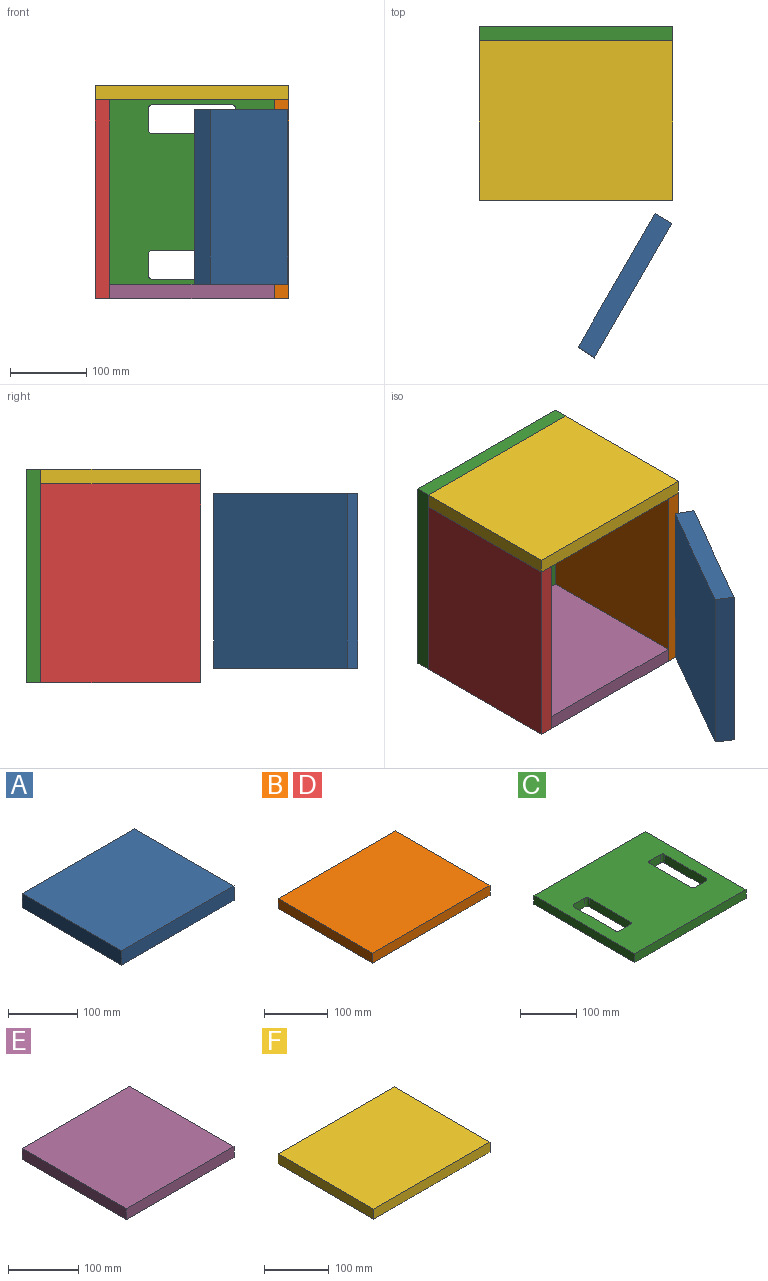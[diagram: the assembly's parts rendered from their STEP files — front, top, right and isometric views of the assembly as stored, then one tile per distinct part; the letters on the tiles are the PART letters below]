
ASSEMBLY  parts=6 mates=5
PART A: 6 faces, bbox 228.6x203.2x25.4 mm
  f0: plane 203.2x25.4mm, normal (-1,0,0), area 5143.3mm2, adj f1,f2,f4,f5
  f1: plane 228.6x201.78mm, normal (0,0,1), area 46127.9mm2, adj f0,f2,f3,f5
  f2: plane 228.6x25.4mm, normal (0,-1,0), area 5806.4mm2, adj f0,f1,f3,f4
  f3: plane 203.2x25.4mm, normal (1,0,0), area 5143.3mm2, adj f1,f2,f4,f5
  f4: plane 228.6x203.2mm, normal (0,0,-1), area 46451.5mm2, adj f0,f2,f3,f5
  f5: plane 228.6x25.4mm, normal (0,1,0.06), area 5815.4mm2, adj f0,f1,f3,f4
PART B: 6 faces, bbox 260.4x209.6x19.1 mm
  f0: plane 260.35x19.05mm, normal (0,1,0), area 4959.7mm2, adj f1,f3,f4,f5
  f1: plane 209.55x19.05mm, normal (-1,0,0), area 3991.9mm2, adj f0,f2,f4,f5
  f2: plane 260.35x19.05mm, normal (0,-1,0), area 4959.7mm2, adj f1,f3,f4,f5
  f3: plane 209.55x19.05mm, normal (1,0,0), area 3991.9mm2, adj f0,f2,f4,f5
  f4: plane 260.35x209.55mm, normal (0,0,1), area 54556.3mm2, adj f0,f1,f2,f3
  f5: plane 260.35x209.55mm, normal (0,0,-1), area 54556.3mm2, adj f0,f1,f2,f3
PART C: 22 faces, bbox 279.4x254x19.1 mm
  f0: plane 279.4x19.05mm, normal (0,1,0), area 5322.6mm2, adj f1,f11,f12,f13
  f1: plane 254x19.05mm, normal (-1,0,0), area 4838.7mm2, adj f0,f2,f12,f13
  f2: plane 279.4x19.05mm, normal (0,-1,0), area 5322.6mm2, adj f1,f11,f12,f13
  f3: plane 104.14x19.05mm, normal (1,0,0), area 1983.9mm2, adj f12,f13,f18,f21
  f4: plane 27.94x19.05mm, normal (0,-1,0), area 532.3mm2, adj f12,f13,f18,f19
  f5: plane 104.14x19.05mm, normal (-1,0,0), area 1983.9mm2, adj f12,f13,f19,f20
  f6: plane 27.94x19.05mm, normal (0,-1,0), area 532.3mm2, adj f12,f13,f14,f17
  f7: plane 104.14x19.05mm, normal (-1,0,0), area 1983.9mm2, adj f12,f13,f14,f15
  f8: plane 27.94x19.05mm, normal (0,1,0), area 532.3mm2, adj f12,f13,f15,f16
  f9: plane 27.94x19.05mm, normal (0,1,0), area 532.3mm2, adj f12,f13,f20,f21
  f10: plane 104.14x19.05mm, normal (1,0,0), area 1983.9mm2, adj f12,f13,f16,f17
  f11: plane 254x19.05mm, normal (1,0,0), area 4838.7mm2, adj f0,f2,f12,f13
  f12: plane 279.4x254mm, normal (0,0,1), area 62302.2mm2, adj f0,f1,f2,f3,f4,f5,f6,f7
  f13: plane 279.4x254mm, normal (0,0,-1), area 62302.2mm2, adj f0,f1,f2,f3,f4,f5,f6,f7
  f14: cylinder r=5.08mm len=19.05mm, axis (0,0,-1), area 152mm2, adj f6,f7,f12,f13
  f15: cylinder r=5.08mm len=19.05mm, axis (0,0,1), area 152mm2, adj f7,f8,f12,f13
  f16: cylinder r=5.08mm len=19.05mm, axis (0,0,-1), area 152mm2, adj f8,f10,f12,f13
  f17: cylinder r=5.08mm len=19.05mm, axis (0,0,1), area 152mm2, adj f6,f10,f12,f13
  f18: cylinder r=5.08mm len=19.05mm, axis (0,0,-1), area 152mm2, adj f3,f4,f12,f13
  f19: cylinder r=5.08mm len=19.05mm, axis (0,0,1), area 152mm2, adj f4,f5,f12,f13
  f20: cylinder r=5.08mm len=19.05mm, axis (0,0,-1), area 152mm2, adj f5,f9,f12,f13
  f21: cylinder r=5.08mm len=19.05mm, axis (0,0,1), area 152mm2, adj f3,f9,f12,f13
PART D: same geometry as B
PART E: 6 faces, bbox 215.9x209.6x19.1 mm
  f0: plane 215.9x19.05mm, normal (0,1,0), area 4112.9mm2, adj f1,f3,f4,f5
  f1: plane 209.55x19.05mm, normal (-1,0,0), area 3991.9mm2, adj f0,f2,f4,f5
  f2: plane 215.9x19.05mm, normal (0,-1,0), area 4112.9mm2, adj f1,f3,f4,f5
  f3: plane 209.55x19.05mm, normal (1,0,0), area 3991.9mm2, adj f0,f2,f4,f5
  f4: plane 215.9x209.55mm, normal (0,0,1), area 45241.8mm2, adj f0,f1,f2,f3
  f5: plane 215.9x209.55mm, normal (0,0,-1), area 45241.8mm2, adj f0,f1,f2,f3
PART F: 6 faces, bbox 254x209.6x19.1 mm
  f0: plane 209.55x19.05mm, normal (-1,0,0), area 3991.9mm2, adj f1,f3,f4,f5
  f1: plane 254x19.05mm, normal (0,-1,0), area 4838.7mm2, adj f0,f2,f4,f5
  f2: plane 209.55x19.05mm, normal (1,0,0), area 3991.9mm2, adj f1,f3,f4,f5
  f3: plane 254x19.05mm, normal (0,1,0), area 4838.7mm2, adj f0,f2,f4,f5
  f4: plane 254x209.55mm, normal (0,0,1), area 53225.7mm2, adj f0,f1,f2,f3
  f5: plane 254x209.55mm, normal (0,0,-1), area 53225.7mm2, adj f0,f1,f2,f3
PLACE A rot(axis=(-0.69,0.19,0.69),158.9deg) t=(-293.02,-859.97,-126.96)mm
PLACE B rot(axis=(0,-1,0),90deg) t=(127,236.88,420.68)mm
PLACE C rot(axis=(0.58,0.58,-0.58),120deg) t=(496.22,123.82,-148.55)mm
PLACE D rot(axis=(0,-1,0),90deg) t=(-107.95,236.88,420.68)mm
PLACE E t=(311.28,-22.69,0)mm
PLACE F t=(292.23,-301.45,260.35)mm
MATE fastened C.f12 <-> E.f0  axis (0,-1,0) through (0,104.78,0)mm
MATE fastened B.f4 <-> E.f3  axis (-1,0,0) through (107.95,0,0)mm
MATE fastened D.f5 <-> E.f1  axis (1,0,0) through (-107.95,0,0)mm
MATE planar A.f3 <-> E.f4  axis (0,0,-1) through (64.04,-216.14,19.05)mm
MATE fastened F.f3 <-> C.f12  axis (0,1,0) through (0,104.78,279.4)mm
